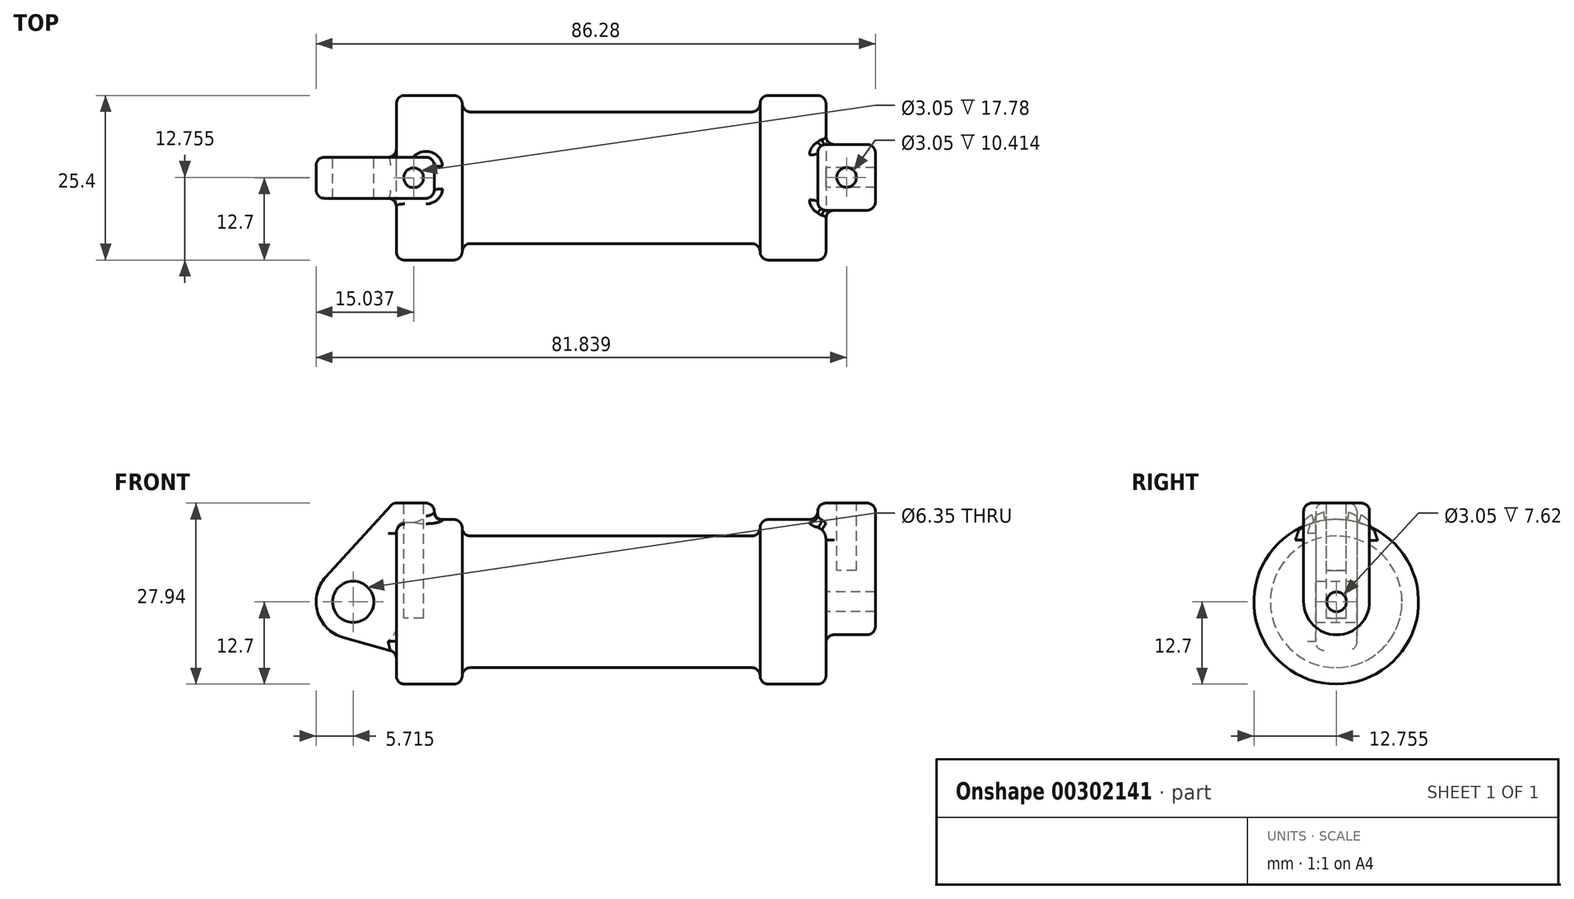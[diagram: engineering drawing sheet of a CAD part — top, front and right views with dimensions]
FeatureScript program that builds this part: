
annotation { "Feature Type Name" : "Feature", "Feature Type Description" : "" }
export const myFeature = defineFeature(function(context is Context, id is Id, definition is map)
    precondition{}
    {
        {
            var Q0;
            Q0=qCreatedBy(makeId("Front.planeOp"),FACE);
            var sketch = newSketch(context, id + "F0", { "sketchPlane" : qUnion([Q0])});
            skLineSegment(sketch, "E0", {"start": v(0, 0) * mm, "end": v(0, 12.7) * mm});
            skLineSegment(sketch, "E1", {"start": v(0, 12.7) * mm, "end": v(10.16, 12.7) * mm});
            skLineSegment(sketch, "E2", {"start": v(10.16, 12.7) * mm, "end": v(10.16, 10.16) * mm});
            skLineSegment(sketch, "E3", {"start": v(10.16, 10.16) * mm, "end": v(56.13, 10.16) * mm});
            skLineSegment(sketch, "E4", {"start": v(56.13, 10.16) * mm, "end": v(56.13, 12.7) * mm});
            skLineSegment(sketch, "E5", {"start": v(56.13, 12.7) * mm, "end": v(66.3, 12.7) * mm});
            skLineSegment(sketch, "E6", {"start": v(66.3, 12.7) * mm, "end": v(66.3, 0) * mm});
            skLineSegment(sketch, "E7", {"start": v(66.3, 0) * mm, "end": v(0, 0) * mm});
            skLineSegment(sketch, "E8", {"start": v(5.84, 15.24) * mm, "end": v(-0.5, 15.24) * mm});
            skLineSegment(sketch, "E9", {"start": v(-0.5, 15.24) * mm, "end": v(-10.88, 3.85) * mm});
            skLineSegment(sketch, "E10", {"start": v(0, 0) * mm, "end": v(-6.65, 0) * mm});
            skCircle(sketch, "E11", {"center": v(-6.65, 0) * mm, "radius": 5.72 * mm});
            skCircle(sketch, "E12", {"center": v(-6.65, 0) * mm, "radius": 3.18 * mm});
            skLineSegment(sketch, "E13", {"start": v(5.84, 15.24) * mm, "end": v(5.84, -9.4) * mm});
            skLineSegment(sketch, "E14", {"start": v(5.84, -9.4) * mm, "end": v(-8.18, -5.5) * mm});
            skSolve(sketch);
        }
        {
            var Q0;
            {var subQ0=sQuery(id+"F0.wireOp",EDGE,"E2");Q0=makeQuery(id+"F0.imprint","IMPRINT",FACE,{"disambiguationData":[TD([[makeQuery(id+"F0.imprint","IMPRINT",EDGE,{"derivedFrom":subQ0}),-1.0]])]});}
            var Q1;
            {var subQ0=sQuery(id+"F0.wireOp",EDGE,"E0");Q1=makeQuery(id+"F0.imprint","IMPRINT",FACE,{"disambiguationData":[TD([[makeQuery(id+"F0.imprint","IMPRINT",EDGE,{"derivedFrom":subQ0}),-1.0]])]});}
            var Q2;
            Q2=sQuery(id+"F0.wireOp",EDGE,"E7");
            revolve(context, id + "F1", {"entities" : qUnion([Q0, Q1]), "axis" : qUnion([Q2]), "revolveType" : RevolveType.FULL});
        }
        {
            var Q0;
            {var subQ5=sQuery(id+"F0.wireOp",EDGE,"E12");Q0=makeQuery(id+"F0.imprint","IMPRINT",FACE,{"disambiguationData":[TD([[makeQuery(id+"F0.imprint","IMPRINT",EDGE,{"derivedFrom":subQ5}),-1.0]])]});}
            var Q1;
            {var subQ1=sQuery(id+"F0.wireOp",EDGE,"E0");Q1=makeQuery(id+"F0.imprint","IMPRINT",FACE,{"disambiguationData":[TD([[makeQuery(id+"F0.imprint","IMPRINT",EDGE,{"derivedFrom":subQ1}),1.0]])]});}
            var Q2;
            {var subQ0=sQuery(id+"F0.wireOp",EDGE,"E14");Q2=makeQuery(id+"F0.imprint","IMPRINT",FACE,{"disambiguationData":[TD([[makeQuery(id+"F0.imprint","IMPRINT",EDGE,{"derivedFrom":subQ0}),-1.0]])]});}
            var Q3;
            {var subQ0=sQuery(id+"F0.wireOp",EDGE,"E0");Q3=makeQuery(id+"F0.imprint","IMPRINT",FACE,{"disambiguationData":[TD([[makeQuery(id+"F0.imprint","IMPRINT",EDGE,{"derivedFrom":subQ0}),-1.0]])]});}
            extrude(context, id + "F2", {"entities" : qUnion([Q0, Q1, Q2, Q3]), "operationType" : NewBodyOperationType.ADD, "endBound" : BoundingType.SYMMETRIC, "depth" : 6.35 * mm});
        }
        {
            var Q0;
            Q0=makeQuery(id+"F1.opRevolve","SWEPT_FACE",FACE,{"disambiguationData":[OSD([sQuery(id+"F0.wireOp",EDGE,"E6")])]});
            var sketch = newSketch(context, id + "F3", { "sketchPlane" : qUnion([Q0])});
            skCircle(sketch, "E15", {"center": v(0.06, 0) * mm, "radius": 1.52 * mm});
            skCircle(sketch, "E16", {"center": v(0.06, 0) * mm, "radius": 5.08 * mm});
            skPoint(sketch, "E17", {"position": v(-5.02, 0) * mm});
            skPoint(sketch, "E18", {"position": v(5.14, 0) * mm});
            skLineSegment(sketch, "E19", {"start": v(-5.02, 0) * mm, "end": v(-5.02, 15.24) * mm});
            skLineSegment(sketch, "E20", {"start": v(5.14, 0) * mm, "end": v(5.14, 15.24) * mm});
            skLineSegment(sketch, "E21", {"start": v(-5.02, 15.24) * mm, "end": v(5.14, 15.24) * mm});
            skSolve(sketch);
        }
        {
            var Q0;
            {var subQ0=sQuery(id+"F3.wireOp",EDGE,"E19");var subQ1=sQuery(id+"F3.wireOp",EDGE,"E16");var subQ2=makeQuery(id+"F3.imprint","INTERSECT",VERTEX,{"derivedFrom":[subQ1,subQ0]});Q0=makeQuery(id+"F3.imprint","IMPRINT",FACE,{"disambiguationData":[TD([[makeQuery(id+"F3.imprint","IMPRINT",EDGE,{"disambiguationData":[TD([[subQ2,1.0]])],"derivedFrom":subQ1}),-1.0]])]});}
            var Q1;
            {var subQ0=sQuery(id+"F3.wireOp",EDGE,"E21");Q1=makeQuery(id+"F3.imprint","IMPRINT",FACE,{"disambiguationData":[TD([[makeQuery(id+"F3.imprint","IMPRINT",EDGE,{"derivedFrom":subQ0}),-1.0]])]});}
            var Q2;
            Q2=makeQuery(id+"F3.imprint","IMPRINT",FACE,{"disambiguationData":[TD([[makeQuery(id+"F3.imprint","IMPRINT",EDGE,{"derivedFrom":sQuery(id+"F3.wireOp",EDGE,"E15")}),-1.0]])]});
            extrude(context, id + "F4", {"entities" : qUnion([Q0, Q1, Q2]), "operationType" : NewBodyOperationType.ADD, "depth" : 7.62 * mm, "hasSecondDirection" : true, "secondDirectionOppositeDirection" : true, "secondDirectionDepth" : 1.27 * mm});
        }
        {
            var Q0;
            Q0=makeQuery(id+"F2.opExtrude","SWEPT_FACE",FACE,{"disambiguationData":[OSD([sQuery(id+"F0.wireOp",EDGE,"E8")])]});
            var sketch = newSketch(context, id + "F5", { "sketchPlane" : qUnion([Q0])});
            skCircle(sketch, "E22", {"center": v(2.67, 0) * mm, "radius": 1.52 * mm});
            skLineSegment(sketch, "E23", {"start": v(73.91, 0.06) * mm, "end": v(73.78, 0.06) * mm});
            skPoint(sketch, "E23.startSnap0", {"position": v(69.47, 0.06) * mm});
            skCircle(sketch, "E24", {"center": v(69.47, 0.06) * mm, "radius": 1.52 * mm});
            skSolve(sketch);
        }
        {
            var Q0;
            Q0=makeQuery(id+"F4.boolean.opBoolean","SPLIT",FACE,{"disambiguationData":[TD([makeQuery(id+"F4.opExtrude","SWEPT_FACE",FACE,{"disambiguationData":[OSD([sQuery(id+"F3.wireOp",EDGE,"E15")])]})])],"derivedFrom":makeQuery(id+"F1.opRevolve","SWEPT_FACE",FACE,{"disambiguationData":[OSD([sQuery(id+"F0.wireOp",EDGE,"E6")])]})});
            var Q1;
            Q1=makeQuery(id+"F1.opRevolve","SWEPT_FACE",FACE,{"disambiguationData":[OSD([sQuery(id+"F0.wireOp",EDGE,"E2")])]});
            extrude(context, id + "F6", {"entities" : qUnion([Q0]), "operationType" : NewBodyOperationType.ADD, "endBound" : BoundingType.UP_TO_SURFACE, "oppositeDirection" : true, "endBoundEntityFace" : qUnion([Q1]), "depth" : 25.4 * mm});
        }
        {
            var Q0;
            Q0=makeQuery(id+"F5.imprint","IMPRINT",FACE,{"disambiguationData":[TD([[makeQuery(id+"F5.imprint","IMPRINT",EDGE,{"derivedFrom":sQuery(id+"F5.wireOp",EDGE,"E22")}),1.0]])]});
            extrude(context, id + "F7", {"entities" : qUnion([Q0]), "operationType" : NewBodyOperationType.REMOVE, "oppositeDirection" : true, "depth" : 17.78 * mm});
        }
        {
            var Q0;
            Q0=makeQuery(id+"F5.imprint","IMPRINT",FACE,{"disambiguationData":[TD([[makeQuery(id+"F5.imprint","IMPRINT",EDGE,{"derivedFrom":sQuery(id+"F5.wireOp",EDGE,"E24")}),1.0]])]});
            extrude(context, id + "F8", {"entities" : qUnion([Q0]), "operationType" : NewBodyOperationType.REMOVE, "oppositeDirection" : true, "depth" : 10.4 * mm});
        }
        {
            var Q0;
            Q0=makeQuery(id+"F1.opRevolve","SWEPT_EDGE",EDGE,{"disambiguationData":[OSD([sQuery(id+"F0.wireOp",EDGE,"E0"),sQuery(id+"F0.wireOp",EDGE,"E1")])]});
            var Q1;
            Q1=makeQuery(id+"F1.opRevolve","SWEPT_EDGE",EDGE,{"disambiguationData":[OSD([sQuery(id+"F0.wireOp",EDGE,"E4"),sQuery(id+"F0.wireOp",EDGE,"E5")])]});
            var Q2;
            Q2=makeQuery(id+"F1.opRevolve","SWEPT_EDGE",EDGE,{"disambiguationData":[OSD([sQuery(id+"F0.wireOp",EDGE,"E5"),sQuery(id+"F0.wireOp",EDGE,"E6")])]});
            var Q3;
            Q3=makeQuery(id+"F1.opRevolve","SWEPT_EDGE",EDGE,{"disambiguationData":[OSD([sQuery(id+"F0.wireOp",EDGE,"E1"),sQuery(id+"F0.wireOp",EDGE,"E2")])]});
            var Q4;
            Q4=makeQuery(id+"F1.opRevolve","SWEPT_EDGE",EDGE,{"disambiguationData":[OSD([sQuery(id+"F0.wireOp",EDGE,"E2"),sQuery(id+"F0.wireOp",EDGE,"E3")])]});
            var Q5;
            Q5=makeQuery(id+"F1.opRevolve","SWEPT_EDGE",EDGE,{"disambiguationData":[OSD([sQuery(id+"F0.wireOp",EDGE,"E3"),sQuery(id+"F0.wireOp",EDGE,"E4")])]});
            fillet(context, id + "F9", {"entities" : qUnion([Q0, Q1, Q2, Q3, Q4, Q5]), "radius" : 1.27 * mm, "tangentPropagation" : true, "allowEdgeOverflow" : false});
        }
        {
            var Q0;
            Q0=makeQuery(id+"F2.opExtrude","CAP_EDGE",EDGE,{"disambiguationData":[OSD([sQuery(id+"F0.wireOp",EDGE,"E9")])],"isStart":true});
            var Q1;
            Q1=makeQuery(id+"F2.opExtrude","SWEPT_FACE",FACE,{"disambiguationData":[OSD([sQuery(id+"F0.wireOp",EDGE,"E9")])]});
            var Q2;
            Q2=makeQuery(id+"F2.opExtrude","SWEPT_FACE",FACE,{"disambiguationData":[OSD([sQuery(id+"F0.wireOp",EDGE,"E11")])]});
            var Q3;
            Q3=makeQuery(id+"F2.opExtrude","CAP_EDGE",EDGE,{"disambiguationData":[OSD([sQuery(id+"F0.wireOp",EDGE,"E14")])],"isStart":true});
            var Q4;
            Q4=makeQuery(id+"F2.opExtrude","SWEPT_FACE",FACE,{"disambiguationData":[OSD([sQuery(id+"F0.wireOp",EDGE,"E14")])]});
            var Q5;
            Q5=makeQuery(id+"F2.opExtrude","CAP_EDGE",EDGE,{"disambiguationData":[OSD([sQuery(id+"F0.wireOp",EDGE,"E11")])],"isStart":false});
            var Q6;
            Q6=makeQuery(id+"F2.boolean.opBoolean","INTERSECT",EDGE,{"derivedFrom":[makeQuery(id+"F1.opRevolve","SWEPT_FACE",FACE,{"disambiguationData":[OSD([sQuery(id+"F0.wireOp",EDGE,"E1")])]}),makeQuery(id+"F2.opExtrude","CAP_FACE",FACE,{"disambiguationData":[OSD([sQuery(id+"F0.wireOp",EDGE,"E8"),sQuery(id+"F0.wireOp",EDGE,"E9"),sQuery(id+"F0.wireOp",EDGE,"E11"),sQuery(id+"F0.wireOp",EDGE,"E12"),sQuery(id+"F0.wireOp",EDGE,"E13"),sQuery(id+"F0.wireOp",EDGE,"E14")])],"isStart":false})]});
            var Q7;
            Q7=makeQuery(id+"F2.opExtrude","CAP_EDGE",EDGE,{"disambiguationData":[OSD([sQuery(id+"F0.wireOp",EDGE,"E8")])],"isStart":true});
            var Q8;
            Q8=makeQuery(id+"F2.opExtrude","SWEPT_EDGE",EDGE,{"disambiguationData":[OSD([sQuery(id+"F0.wireOp",EDGE,"E8"),sQuery(id+"F0.wireOp",EDGE,"E13")])]});
            var Q9;
            Q9=makeQuery(id+"F2.opExtrude","CAP_EDGE",EDGE,{"disambiguationData":[OSD([sQuery(id+"F0.wireOp",EDGE,"E8")])],"isStart":false});
            var Q10;
            Q10=makeQuery(id+"F2.boolean.opBoolean","INTERSECT",EDGE,{"derivedFrom":[makeQuery(id+"F1.opRevolve","SWEPT_FACE",FACE,{"disambiguationData":[OSD([sQuery(id+"F0.wireOp",EDGE,"E1")])]}),makeQuery(id+"F2.opExtrude","SWEPT_FACE",FACE,{"disambiguationData":[OSD([sQuery(id+"F0.wireOp",EDGE,"E13")])]})]});
            var Q11;
            Q11=makeQuery(id+"F2.opExtrude","CAP_EDGE",EDGE,{"disambiguationData":[OSD([sQuery(id+"F0.wireOp",EDGE,"E13")])],"isStart":false});
            var Q12;
            Q12=makeQuery(id+"F2.opExtrude","CAP_EDGE",EDGE,{"disambiguationData":[OSD([sQuery(id+"F0.wireOp",EDGE,"E13")])],"isStart":true});
            fillet(context, id + "F10", {"entities" : qUnion([Q0, Q1, Q2, Q3, Q4, Q5, Q6, Q7, Q8, Q9, Q10, Q11, Q12]), "radius" : 1.27 * mm, "tangentPropagation" : true, "allowEdgeOverflow" : false});
        }
        {
            var Q0;
            Q0=makeQuery(id+"F4.opExtrude","SWEPT_EDGE",EDGE,{"disambiguationData":[OSD([sQuery(id+"F3.wireOp",EDGE,"E19"),sQuery(id+"F3.wireOp",EDGE,"E21")])]});
            var Q1;
            Q1=makeQuery(id+"F4.opExtrude","CAP_EDGE",EDGE,{"disambiguationData":[OSD([sQuery(id+"F3.wireOp",EDGE,"E19")])],"isStart":true});
            var Q2;
            Q2=makeQuery(id+"F4.opExtrude","CAP_EDGE",EDGE,{"disambiguationData":[OSD([sQuery(id+"F3.wireOp",EDGE,"E19")])],"isStart":false});
            var Q3;
            Q3=makeQuery(id+"F4.opExtrude","CAP_EDGE",EDGE,{"disambiguationData":[OSD([sQuery(id+"F3.wireOp",EDGE,"E21")])],"isStart":false});
            var Q4;
            Q4=makeQuery(id+"F4.opExtrude","CAP_EDGE",EDGE,{"disambiguationData":[OSD([sQuery(id+"F3.wireOp",EDGE,"E16")])],"isStart":false});
            var Q5;
            Q5=makeQuery(id+"F4.boolean.opBoolean","INTERSECT",EDGE,{"derivedFrom":[makeQuery(id+"F1.opRevolve","SWEPT_FACE",FACE,{"disambiguationData":[OSD([sQuery(id+"F0.wireOp",EDGE,"E6")])]}),makeQuery(id+"F4.opExtrude","SWEPT_FACE",FACE,{"disambiguationData":[OSD([sQuery(id+"F3.wireOp",EDGE,"E19")])]})]});
            var Q6;
            Q6=makeQuery(id+"F9.opFillet","BLEND_EDGE",EDGE,{"blendedFrom":[makeQuery(id+"F1.opRevolve","SWEPT_EDGE",EDGE,{"disambiguationData":[OSD([sQuery(id+"F0.wireOp",EDGE,"E5"),sQuery(id+"F0.wireOp",EDGE,"E6")])]}),makeQuery(id+"F4.opExtrude","SWEPT_FACE",FACE,{"disambiguationData":[OSD([sQuery(id+"F3.wireOp",EDGE,"E19")])]})],"blendedInto":[makeQuery(id+"F4.opExtrude","SWEPT_FACE",FACE,{"disambiguationData":[OSD([sQuery(id+"F3.wireOp",EDGE,"E19")])]})]});
            var Q7;
            Q7=makeQuery(id+"F4.boolean.opBoolean","INTERSECT",EDGE,{"derivedFrom":[makeQuery(id+"F1.opRevolve","SWEPT_FACE",FACE,{"disambiguationData":[OSD([sQuery(id+"F0.wireOp",EDGE,"E6")])]}),makeQuery(id+"F4.opExtrude","SWEPT_FACE",FACE,{"disambiguationData":[OSD([sQuery(id+"F3.wireOp",EDGE,"E16")])]})]});
            var Q8;
            Q8=makeQuery(id+"F4.boolean.opBoolean","INTERSECT",EDGE,{"derivedFrom":[makeQuery(id+"F1.opRevolve","SWEPT_FACE",FACE,{"disambiguationData":[OSD([sQuery(id+"F0.wireOp",EDGE,"E6")])]}),makeQuery(id+"F4.opExtrude","SWEPT_FACE",FACE,{"disambiguationData":[OSD([sQuery(id+"F3.wireOp",EDGE,"E20")])]})]});
            var Q9;
            Q9=makeQuery(id+"F9.opFillet","BLEND_EDGE",EDGE,{"blendedFrom":[makeQuery(id+"F1.opRevolve","SWEPT_EDGE",EDGE,{"disambiguationData":[OSD([sQuery(id+"F0.wireOp",EDGE,"E5"),sQuery(id+"F0.wireOp",EDGE,"E6")])]}),makeQuery(id+"F4.opExtrude","SWEPT_FACE",FACE,{"disambiguationData":[OSD([sQuery(id+"F3.wireOp",EDGE,"E20")])]})],"blendedInto":[makeQuery(id+"F4.opExtrude","SWEPT_FACE",FACE,{"disambiguationData":[OSD([sQuery(id+"F3.wireOp",EDGE,"E20")])]})]});
            var Q10;
            Q10=makeQuery(id+"F4.opExtrude","CAP_EDGE",EDGE,{"disambiguationData":[OSD([sQuery(id+"F3.wireOp",EDGE,"E20")])],"isStart":true});
            var Q11;
            Q11=makeQuery(id+"F4.opExtrude","CAP_EDGE",EDGE,{"disambiguationData":[OSD([sQuery(id+"F3.wireOp",EDGE,"E20")])],"isStart":false});
            var Q12;
            Q12=makeQuery(id+"F4.opExtrude","SWEPT_EDGE",EDGE,{"disambiguationData":[OSD([sQuery(id+"F3.wireOp",EDGE,"E20"),sQuery(id+"F3.wireOp",EDGE,"E21")])]});
            var Q13;
            Q13=makeQuery(id+"F4.opExtrude","CAP_EDGE",EDGE,{"disambiguationData":[OSD([sQuery(id+"F3.wireOp",EDGE,"E21")])],"isStart":true});
            var Q14;
            Q14=makeQuery(id+"F4.boolean.opBoolean","INTERSECT",EDGE,{"derivedFrom":[makeQuery(id+"F1.opRevolve","SWEPT_FACE",FACE,{"disambiguationData":[OSD([sQuery(id+"F0.wireOp",EDGE,"E5")])]}),makeQuery(id+"F4.opExtrude","CAP_FACE",FACE,{"disambiguationData":[OSD([sQuery(id+"F3.wireOp",EDGE,"E15"),sQuery(id+"F3.wireOp",EDGE,"E16"),sQuery(id+"F3.wireOp",EDGE,"E19"),sQuery(id+"F3.wireOp",EDGE,"E20"),sQuery(id+"F3.wireOp",EDGE,"E21")])],"isStart":true})]});
            fillet(context, id + "F11", {"entities" : qUnion([Q0, Q1, Q2, Q3, Q4, Q5, Q6, Q7, Q8, Q9, Q10, Q11, Q12, Q13, Q14]), "radius" : 1.27 * mm, "tangentPropagation" : true, "allowEdgeOverflow" : false});
        }
    });
